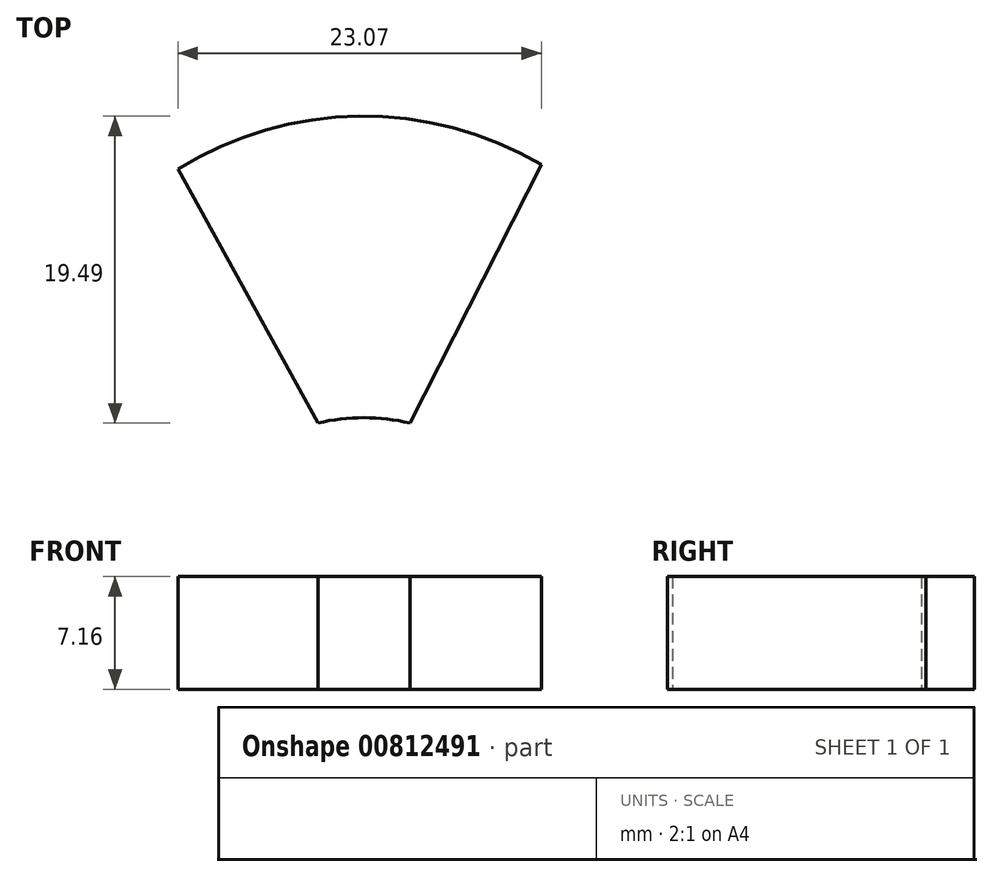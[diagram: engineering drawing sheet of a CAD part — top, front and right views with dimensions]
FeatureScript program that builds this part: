
annotation { "Feature Type Name" : "Feature", "Feature Type Description" : "" }
export const myFeature = defineFeature(function(context is Context, id is Id, definition is map)
    precondition{}
    {
        {
            var Q0;
            Q0=qCreatedBy(makeId("Top.planeOp"),FACE);
            var sketch = newSketch(context, id + "F0", { "sketchPlane" : qUnion([Q0])});
            skArc(sketch, "E0", {"start": v(5.84, 0) * mm, "mid": v(2.92, 0.34) * mm, "end": v(0, 0) * mm});
            skLineSegment(sketch, "E1", {"start": v(0, 0) * mm, "end": v(-8.88, 16.13) * mm});
            skLineSegment(sketch, "E2", {"start": v(5.84, 0) * mm, "end": v(14.19, 16.41) * mm});
            skArc(sketch, "E3", {"start": v(14.19, 16.41) * mm, "mid": v(2.61, 19.5) * mm, "end": v(-8.88, 16.13) * mm});
            skSolve(sketch);
        }
        {
            var Q0;
            Q0=makeQuery(id+"F0.imprint","IMPRINT",FACE,{"disambiguationData":[TD([[makeQuery(id+"F0.imprint","IMPRINT",EDGE,{"derivedFrom":sQuery(id+"F0.wireOp",EDGE,"E0")}),-1.0]])]});
            extrude(context, id + "F1", {"entities" : qUnion([Q0]), "depth" : 7.16 * mm, "offsetDistance" : 25.4 * mm});
        }
    });
